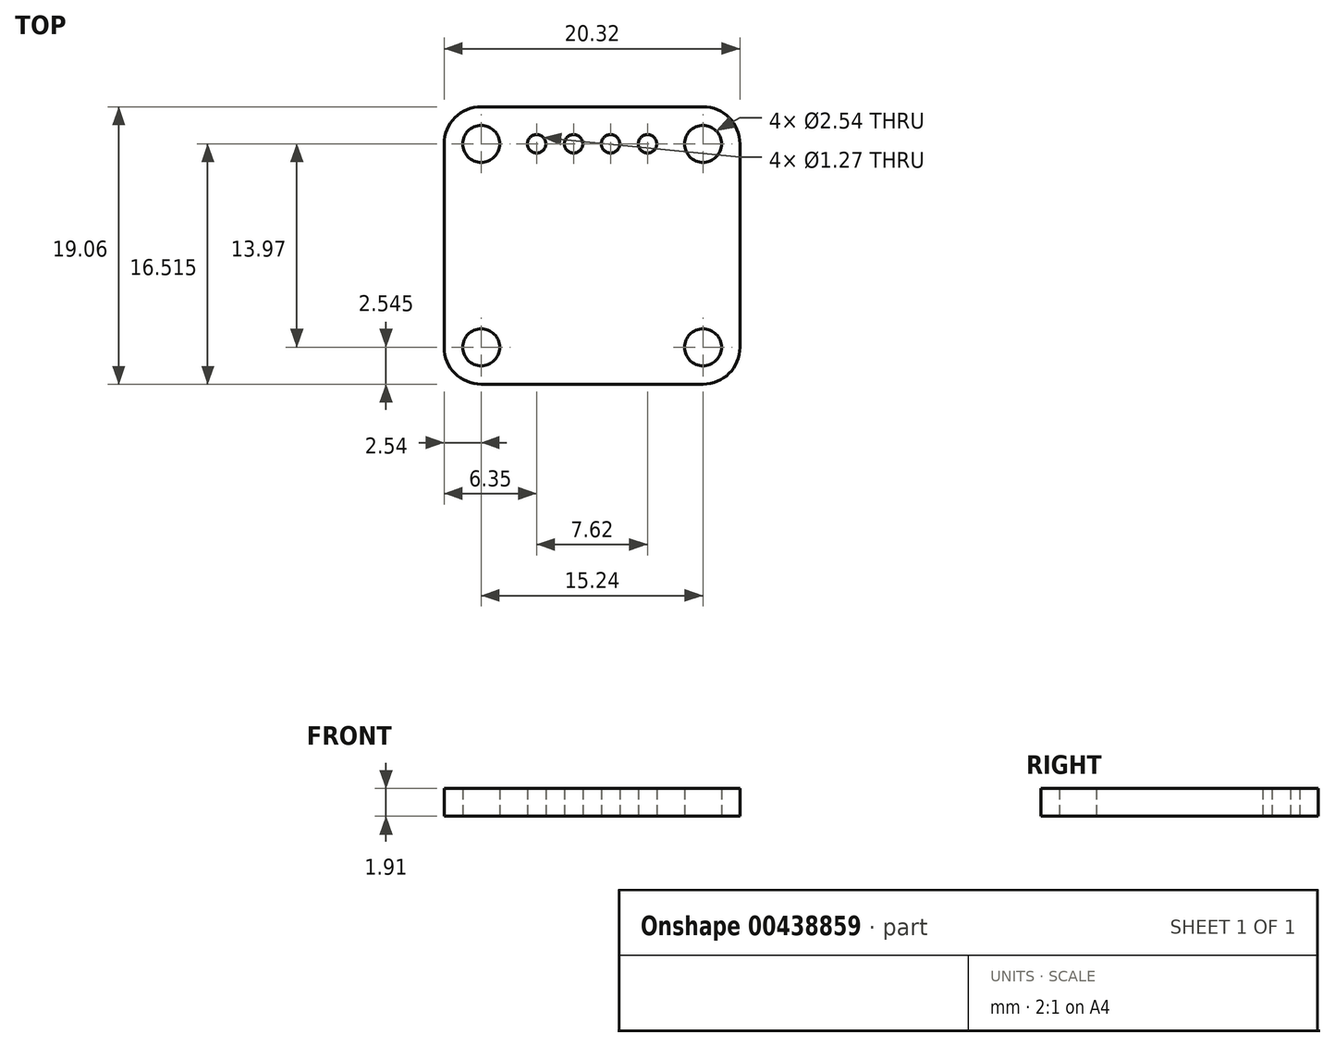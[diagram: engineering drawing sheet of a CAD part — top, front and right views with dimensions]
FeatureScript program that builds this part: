
annotation { "Feature Type Name" : "Feature", "Feature Type Description" : "" }
export const myFeature = defineFeature(function(context is Context, id is Id, definition is map)
    precondition{}
    {
        {
            var Q0;
            Q0=qCreatedBy(makeId("Top.planeOp"),FACE);
            var sketch = newSketch(context, id + "F0", { "sketchPlane" : qUnion([Q0])});
            skLineSegment(sketch, "E0.bottom", {"start": v(10.16, -9.52) * mm, "end": v(-10.16, -9.53) * mm});
            skLineSegment(sketch, "E0.top", {"start": v(10.16, 9.53) * mm, "end": v(-10.16, 9.52) * mm});
            skLineSegment(sketch, "E0.left", {"start": v(10.16, -9.52) * mm, "end": v(10.16, 9.53) * mm});
            skLineSegment(sketch, "E0.right", {"start": v(-10.16, -9.53) * mm, "end": v(-10.16, 9.52) * mm});
            skPoint(sketch, "E0.middle", {"position": v(0, 0) * mm});
            skLineSegment(sketch, "E1.bottom", {"start": v(7.62, -6.99) * mm, "end": v(-7.62, -6.99) * mm, "construction": true});
            skLineSegment(sketch, "E1.top", {"start": v(7.62, 6.98) * mm, "end": v(-7.62, 6.99) * mm, "construction": true});
            skLineSegment(sketch, "E1.left", {"start": v(7.62, -6.99) * mm, "end": v(7.62, 6.99) * mm, "construction": true});
            skLineSegment(sketch, "E1.right", {"start": v(-7.62, -6.99) * mm, "end": v(-7.62, 6.99) * mm, "construction": true});
            skCircle(sketch, "E2", {"center": v(-7.62, -6.99) * mm, "radius": 1.27 * mm});
            skCircle(sketch, "E3.0.1.0", {"center": v(-7.62, 6.99) * mm, "radius": 1.27 * mm});
            skCircle(sketch, "E3.1.0.0", {"center": v(7.62, -6.99) * mm, "radius": 1.27 * mm});
            skCircle(sketch, "E3.1.1.0", {"center": v(7.62, 6.99) * mm, "radius": 1.27 * mm});
            skLineSegment(sketch, "E3.direction1", {"start": v(-7.62, -6.99) * mm, "end": v(7.62, -6.99) * mm, "construction": true});
            skArc(sketch, "E4", {"start": v(-7.62, -9.53) * mm, "mid": v(-9.42, -8.78) * mm, "end": v(-10.16, -6.99) * mm});
            skArc(sketch, "E5", {"start": v(7.62, -9.52) * mm, "mid": v(9.42, -8.78) * mm, "end": v(10.16, -6.99) * mm});
            skArc(sketch, "E6", {"start": v(10.16, 6.98) * mm, "mid": v(9.42, 8.78) * mm, "end": v(7.62, 9.53) * mm});
            skArc(sketch, "E7", {"start": v(-10.16, 6.99) * mm, "mid": v(-9.42, 8.78) * mm, "end": v(-7.62, 9.53) * mm});
            skCircle(sketch, "E8", {"center": v(-3.81, 6.99) * mm, "radius": 0.64 * mm});
            skCircle(sketch, "E9.1.0.0", {"center": v(-1.27, 6.99) * mm, "radius": 0.64 * mm});
            skCircle(sketch, "E9.2.0.0", {"center": v(1.27, 6.99) * mm, "radius": 0.64 * mm});
            skCircle(sketch, "E9.3.0.0", {"center": v(3.81, 6.99) * mm, "radius": 0.64 * mm});
            skLineSegment(sketch, "E9.direction1", {"start": v(-3.81, 6.99) * mm, "end": v(-1.27, 6.99) * mm, "construction": true});
            skLineSegment(sketch, "E10", {"start": v(-1.27, 6.99) * mm, "end": v(1.27, 6.99) * mm, "construction": true});
            skPoint(sketch, "E11", {"position": v(0, 6.99) * mm});
            skSolve(sketch);
        }
        {
            var Q0;
            Q0=makeQuery(id+"F0.imprint","IMPRINT",FACE,{"disambiguationData":[TD([[makeQuery(id+"F0.imprint","IMPRINT",EDGE,{"derivedFrom":sQuery(id+"F0.wireOp",EDGE,"E2")}),-1.0]])]});
            extrude(context, id + "F1", {"entities" : qUnion([Q0]), "depth" : 1.9 * mm, "offsetDistance" : 25.4 * mm});
        }
    });
